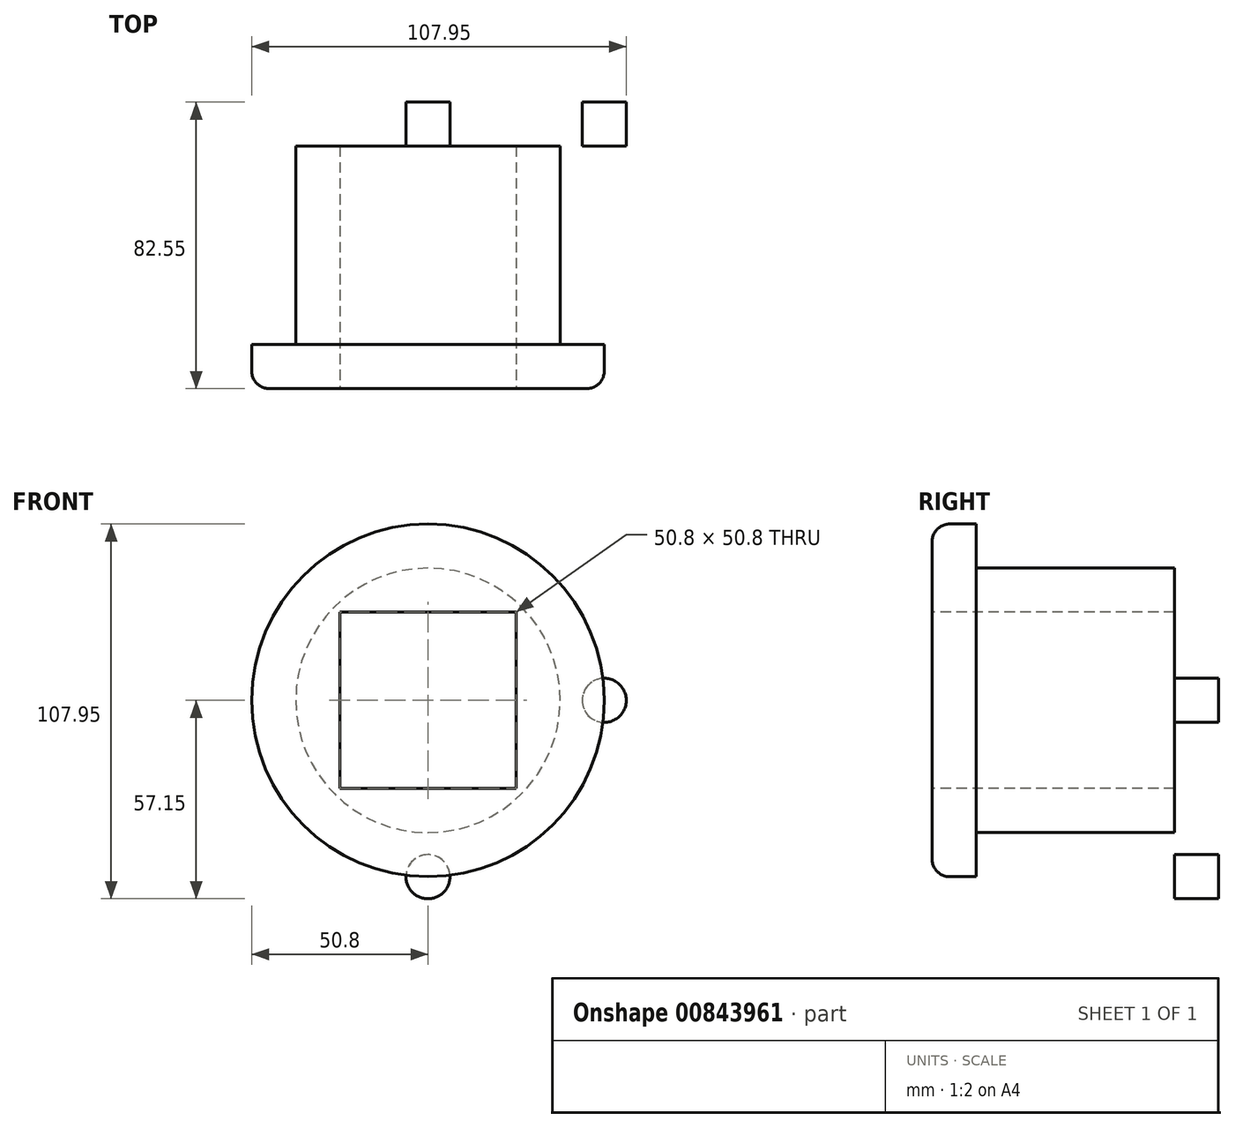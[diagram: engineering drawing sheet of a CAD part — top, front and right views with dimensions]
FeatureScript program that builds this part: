
annotation { "Feature Type Name" : "Feature", "Feature Type Description" : "" }
export const myFeature = defineFeature(function(context is Context, id is Id, definition is map)
    precondition{}
    {
        {
            var Q0;
            Q0=qCreatedBy(makeId("Front.planeOp"),FACE);
            var sketch = newSketch(context, id + "F0", { "sketchPlane" : qUnion([Q0])});
            skCircle(sketch, "E0", {"center": v(0, 0) * mm, "radius": 63.5 * mm});
            skSolve(sketch);
        }
        {
            var Q0;
            Q0 = qSketchRegion(id + "F0", true);
            extrude(context, id + "F1", {"entities" : qUnion([Q0]), "depth" : 12.7 * mm, "offsetDistance" : 25.4 * mm});
        }
        {
            var Q0;
            Q0=makeQuery(id+"F1.opExtrude","CAP_FACE",FACE,{"disambiguationData":[OSD([sQuery(id+"F0.wireOp",EDGE,"E0")])],"isStart":false});
            var sketch = newSketch(context, id + "F2", { "sketchPlane" : qUnion([Q0])});
            skCircle(sketch, "E1", {"center": v(0, 0) * mm, "radius": 50.8 * mm});
            skCircle(sketch, "E2", {"center": v(0, 50.8) * mm, "radius": 6.35 * mm});
            skCircle(sketch, "E3", {"center": v(-50.8, 0) * mm, "radius": 6.35 * mm});
            skCircle(sketch, "E4", {"center": v(0, -50.8) * mm, "radius": 6.35 * mm});
            skCircle(sketch, "E5", {"center": v(50.8, 0) * mm, "radius": 6.35 * mm});
            skSolve(sketch);
        }
        {
            var Q0;
            {var subQ0=sQuery(id+"F2.wireOp",EDGE,"E3");var subQ1=sQuery(id+"F2.wireOp",EDGE,"E1");var subQ2=makeQuery(id+"F2.imprint","INTERSECT",VERTEX,{"disambiguationData":[OD(0.0)],"derivedFrom":[subQ1,subQ0]});Q0=makeQuery(id+"F2.imprint","IMPRINT",FACE,{"disambiguationData":[TD([[makeQuery(id+"F2.imprint","IMPRINT",EDGE,{"disambiguationData":[TD([[subQ2,-1.0]])],"derivedFrom":subQ1}),-1.0]])]});}
            var Q1;
            {var subQ0=sQuery(id+"F2.wireOp",EDGE,"E3");var subQ1=sQuery(id+"F2.wireOp",EDGE,"E1");var subQ2=makeQuery(id+"F2.imprint","INTERSECT",VERTEX,{"disambiguationData":[OD(0.0)],"derivedFrom":[subQ1,subQ0]});Q1=makeQuery(id+"F2.imprint","IMPRINT",FACE,{"disambiguationData":[TD([[makeQuery(id+"F2.imprint","IMPRINT",EDGE,{"disambiguationData":[TD([[subQ2,-1.0]])],"derivedFrom":subQ1}),1.0]])]});}
            var Q2;
            {var subQ0=sQuery(id+"F2.wireOp",EDGE,"E2");var subQ1=sQuery(id+"F2.wireOp",EDGE,"E1");var subQ2=makeQuery(id+"F2.imprint","INTERSECT",VERTEX,{"disambiguationData":[OD(0.0)],"derivedFrom":[subQ1,subQ0]});Q2=makeQuery(id+"F2.imprint","IMPRINT",FACE,{"disambiguationData":[TD([[makeQuery(id+"F2.imprint","IMPRINT",EDGE,{"disambiguationData":[TD([[subQ2,-1.0]])],"derivedFrom":subQ1}),1.0]])]});}
            var Q3;
            {var subQ0=sQuery(id+"F2.wireOp",EDGE,"E2");var subQ1=sQuery(id+"F2.wireOp",EDGE,"E1");var subQ2=makeQuery(id+"F2.imprint","INTERSECT",VERTEX,{"disambiguationData":[OD(0.0)],"derivedFrom":[subQ1,subQ0]});Q3=makeQuery(id+"F2.imprint","IMPRINT",FACE,{"disambiguationData":[TD([[makeQuery(id+"F2.imprint","IMPRINT",EDGE,{"disambiguationData":[TD([[subQ2,-1.0]])],"derivedFrom":subQ1}),-1.0]])]});}
            var Q4;
            {var subQ0=sQuery(id+"F2.wireOp",EDGE,"E5");var subQ1=sQuery(id+"F2.wireOp",EDGE,"E1");var subQ2=makeQuery(id+"F2.imprint","INTERSECT",VERTEX,{"disambiguationData":[OD(0.0)],"derivedFrom":[subQ1,subQ0]});Q4=makeQuery(id+"F2.imprint","IMPRINT",FACE,{"disambiguationData":[TD([[makeQuery(id+"F2.imprint","IMPRINT",EDGE,{"disambiguationData":[TD([[subQ2,1.0]])],"derivedFrom":subQ1}),1.0]])]});}
            var Q5;
            {var subQ0=sQuery(id+"F2.wireOp",EDGE,"E5");var subQ1=sQuery(id+"F2.wireOp",EDGE,"E1");var subQ2=makeQuery(id+"F2.imprint","INTERSECT",VERTEX,{"disambiguationData":[OD(0.0)],"derivedFrom":[subQ1,subQ0]});Q5=makeQuery(id+"F2.imprint","IMPRINT",FACE,{"disambiguationData":[TD([[makeQuery(id+"F2.imprint","IMPRINT",EDGE,{"disambiguationData":[TD([[subQ2,1.0]])],"derivedFrom":subQ1}),-1.0]])]});}
            var Q6;
            {var subQ0=sQuery(id+"F2.wireOp",EDGE,"E4");var subQ1=sQuery(id+"F2.wireOp",EDGE,"E1");var subQ2=makeQuery(id+"F2.imprint","INTERSECT",VERTEX,{"disambiguationData":[OD(0.0)],"derivedFrom":[subQ1,subQ0]});Q6=makeQuery(id+"F2.imprint","IMPRINT",FACE,{"disambiguationData":[TD([[makeQuery(id+"F2.imprint","IMPRINT",EDGE,{"disambiguationData":[TD([[subQ2,-1.0]])],"derivedFrom":subQ1}),1.0]])]});}
            var Q7;
            {var subQ0=sQuery(id+"F2.wireOp",EDGE,"E4");var subQ1=sQuery(id+"F2.wireOp",EDGE,"E1");var subQ2=makeQuery(id+"F2.imprint","INTERSECT",VERTEX,{"disambiguationData":[OD(0.0)],"derivedFrom":[subQ1,subQ0]});Q7=makeQuery(id+"F2.imprint","IMPRINT",FACE,{"disambiguationData":[TD([[makeQuery(id+"F2.imprint","IMPRINT",EDGE,{"disambiguationData":[TD([[subQ2,-1.0]])],"derivedFrom":subQ1}),-1.0]])]});}
            extrude(context, id + "F3", {"entities" : qUnion([Q0, Q1, Q2, Q3, Q4, Q5, Q6, Q7]), "operationType" : NewBodyOperationType.REMOVE, "oppositeDirection" : true, "depth" : 25.4 * mm, "offsetDistance" : 25.4 * mm});
        }
        {
            var Q0;
            Q0=makeQuery(id+"F1.opExtrude","CAP_FACE",FACE,{"disambiguationData":[OSD([sQuery(id+"F0.wireOp",EDGE,"E0")])],"isStart":false});
            var sketch = newSketch(context, id + "F4", { "sketchPlane" : qUnion([Q0])});
            skCircle(sketch, "E6", {"center": v(0, 0) * mm, "radius": 38.1 * mm});
            skSolve(sketch);
        }
        {
            var Q0;
            Q0=makeQuery(id+"F4.imprint","IMPRINT",FACE,{"disambiguationData":[TD([[makeQuery(id+"F4.imprint","IMPRINT",EDGE,{"derivedFrom":sQuery(id+"F4.wireOp",EDGE,"E6")}),1.0]])]});
            extrude(context, id + "F5", {"entities" : qUnion([Q0]), "operationType" : NewBodyOperationType.ADD, "depth" : 57.15 * mm, "offsetDistance" : 25.4 * mm});
        }
        {
            var Q0;
            Q0=makeQuery(id+"F5.opExtrude","CAP_FACE",FACE,{"disambiguationData":[OSD([sQuery(id+"F4.wireOp",EDGE,"E6")])],"isStart":false});
            var sketch = newSketch(context, id + "F6", { "sketchPlane" : qUnion([Q0])});
            skCircle(sketch, "E7", {"center": v(0, 0) * mm, "radius": 50.8 * mm});
            skSolve(sketch);
        }
        {
            var Q0;
            Q0 = qSketchRegion(id + "F6", true);
            extrude(context, id + "F7", {"entities" : qUnion([Q0]), "operationType" : NewBodyOperationType.ADD, "depth" : 12.7 * mm, "offsetDistance" : 25.4 * mm});
        }
        {
            var Q0;
            Q0=makeQuery(id+"F7.opExtrude","CAP_FACE",FACE,{"disambiguationData":[OSD([sQuery(id+"F6.wireOp",EDGE,"E7")])],"isStart":false});
            fillet(context, id + "F8", {"entities" : qUnion([Q0]), "radius" : 5.08 * mm, "tangentPropagation" : true, "allowEdgeOverflow" : false});
        }
        {
            var Q0;
            Q0=makeQuery(id+"F7.opExtrude","CAP_FACE",FACE,{"disambiguationData":[OSD([sQuery(id+"F6.wireOp",EDGE,"E7")])],"isStart":false});
            var sketch = newSketch(context, id + "F9", { "sketchPlane" : qUnion([Q0])});
            skLineSegment(sketch, "E8", {"start": v(-25.4, 25.4) * mm, "end": v(25.4, 25.4) * mm});
            skLineSegment(sketch, "E9", {"start": v(-25.4, 25.4) * mm, "end": v(-25.4, -25.4) * mm});
            skLineSegment(sketch, "E10", {"start": v(-25.4, -25.4) * mm, "end": v(25.4, -25.4) * mm});
            skLineSegment(sketch, "E11", {"start": v(25.4, -25.4) * mm, "end": v(25.4, 25.4) * mm});
            skSolve(sketch);
        }
        {
            var Q0;
            Q0=makeQuery(id+"F9.imprint","IMPRINT",FACE,{"disambiguationData":[TD([[makeQuery(id+"F9.imprint","IMPRINT",EDGE,{"derivedFrom":sQuery(id+"F9.wireOp",EDGE,"E8")}),-1.0]])]});
            var sketch = newSketch(context, id + "F10", { "sketchPlane" : qUnion([Q0])});
            skSolve(sketch);
        }
        {
            var Q0;
            Q0=makeQuery(id+"F10.imprint","IMPRINT",FACE,{"disambiguationData":[TD([[makeQuery(id+"F10.imprint","IMPRINT",EDGE,{"derivedFrom":makeQuery(id+"F9.imprint","IMPRINT",EDGE,{"derivedFrom":sQuery(id+"F9.wireOp",EDGE,"E8")})}),-1.0]])]});
            extrude(context, id + "F11", {"entities" : qUnion([Q0]), "operationType" : NewBodyOperationType.REMOVE, "oppositeDirection" : true, "depth" : 127 * mm, "offsetDistance" : 25.4 * mm});
        }
    });
